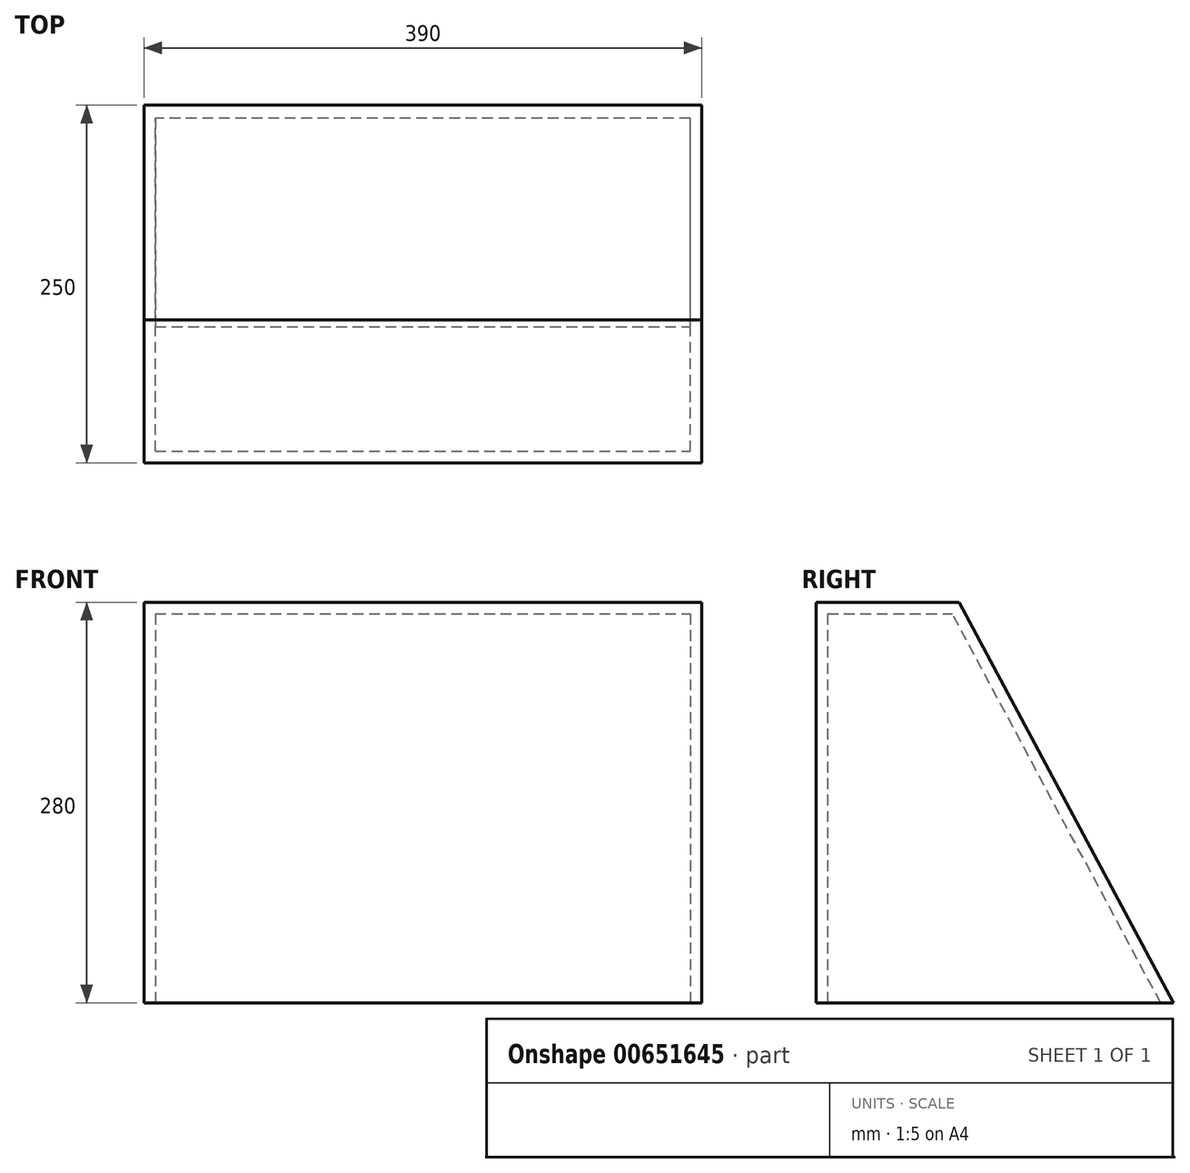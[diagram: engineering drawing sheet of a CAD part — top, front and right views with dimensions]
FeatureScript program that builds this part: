
annotation { "Feature Type Name" : "Feature", "Feature Type Description" : "" }
export const myFeature = defineFeature(function(context is Context, id is Id, definition is map)
    precondition{}
    {
        {
            assignVariable(context, id + "F0", {"name" : "d", "anyValue" : 8});
        }
        {
            assignVariable(context, id + "F1", {"name" : "h", "anyValue" : 280});
        }
        {
            assignVariable(context, id + "F2", {"name" : "bottom_t", "anyValue" : 100});
        }
        {
            assignVariable(context, id + "F3", {"name" : "top_t", "anyValue" : 250});
        }
        {
            var Q0;
            Q0=qCreatedBy(makeId("Top.planeOp"),FACE);
            var sketch = newSketch(context, id + "F4", { "sketchPlane" : qUnion([Q0])});
            skLineSegment(sketch, "E0.bottom", {"start": v(-185.14, -178.03) * mm, "end": v(204.86, -178.03) * mm});
            skLineSegment(sketch, "E0.top", {"start": v(-185.14, 71.97) * mm, "end": v(204.86, 71.97) * mm});
            skLineSegment(sketch, "E0.left", {"start": v(-185.14, -178.03) * mm, "end": v(-185.14, 71.97) * mm});
            skLineSegment(sketch, "E0.right", {"start": v(204.86, -178.03) * mm, "end": v(204.86, 71.97) * mm});
            skSolve(sketch);
        }
        {
            var Q0;
            Q0=makeQuery(id+"F4.imprint","IMPRINT",FACE,{"disambiguationData":[TD([[makeQuery(id+"F4.imprint","IMPRINT",EDGE,{"derivedFrom":sQuery(id+"F4.wireOp",EDGE,"E0.bottom")}),1.0]])]});
            extrude(context, id + "F5", {"entities" : qUnion([Q0]), "depth" : (getVariable(context, 'h')) * mm, "offsetDistance" : 25 * mm});
        }
        {
            var Q0;
            Q0=makeQuery(id+"F5.opExtrude","CAP_EDGE",EDGE,{"disambiguationData":[OSD([sQuery(id+"F4.wireOp",EDGE,"E0.top")])],"isStart":false});
            chamfer(context, id + "F6", {"entities" : qUnion([Q0]), "chamferType" : ChamferType.TWO_OFFSETS, "width1" : (getVariable(context, 'h')) * mm, "oppositeDirection" : false, "width2" : (getVariable(context, 'top_t') - getVariable(context, 'bottom_t')) * mm, "tangentPropagation" : true});
        }
        {
            var Q0;
            Q0=makeQuery(id+"F5.opExtrude","CAP_FACE",FACE,{"disambiguationData":[OSD([sQuery(id+"F4.wireOp",EDGE,"E0.bottom"),sQuery(id+"F4.wireOp",EDGE,"E0.top"),sQuery(id+"F4.wireOp",EDGE,"E0.left"),sQuery(id+"F4.wireOp",EDGE,"E0.right")])],"isStart":true});
            shell(context, id + "F7", {"entities" : qUnion([Q0]), "thickness" : (getVariable(context, 'd')) * mm});
        }
    });
